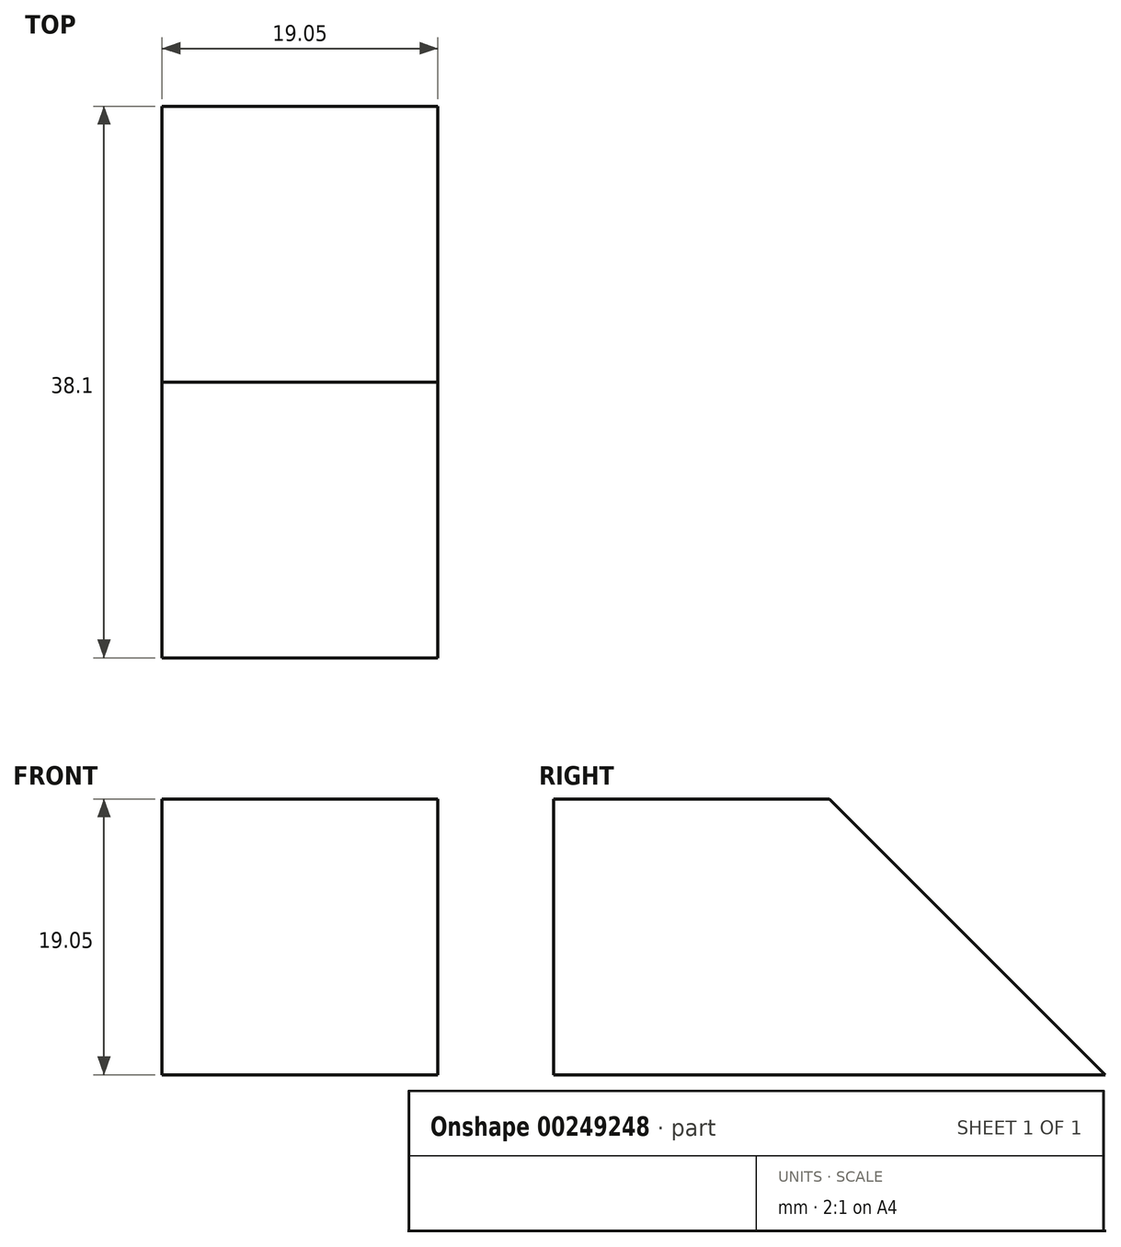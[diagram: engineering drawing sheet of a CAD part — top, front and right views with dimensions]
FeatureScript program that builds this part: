
annotation { "Feature Type Name" : "Feature", "Feature Type Description" : "" }
export const myFeature = defineFeature(function(context is Context, id is Id, definition is map)
    precondition{}
    {
        {
            var Q0;
            Q0=qCreatedBy(makeId("Right.planeOp"),FACE);
            var sketch = newSketch(context, id + "F0", { "sketchPlane" : qUnion([Q0])});
            skLineSegment(sketch, "E0", {"start": v(0, 0) * mm, "end": v(0, 19.05) * mm});
            skLineSegment(sketch, "E1", {"start": v(0, 0) * mm, "end": v(38.1, 0) * mm});
            skLineSegment(sketch, "E2", {"start": v(0, 19.05) * mm, "end": v(19.05, 19.05) * mm});
            skLineSegment(sketch, "E3", {"start": v(19.05, 19.05) * mm, "end": v(38.1, 0) * mm});
            skSolve(sketch);
        }
        {
            var Q0;
            Q0=makeQuery(id+"F0.imprint","IMPRINT",FACE,{"disambiguationData":[TD([[makeQuery(id+"F0.imprint","IMPRINT",EDGE,{"derivedFrom":sQuery(id+"F0.wireOp",EDGE,"E0")}),-1.0]])]});
            extrude(context, id + "F1", {"entities" : qUnion([Q0]), "depth" : 19.05 * mm});
        }
    });
